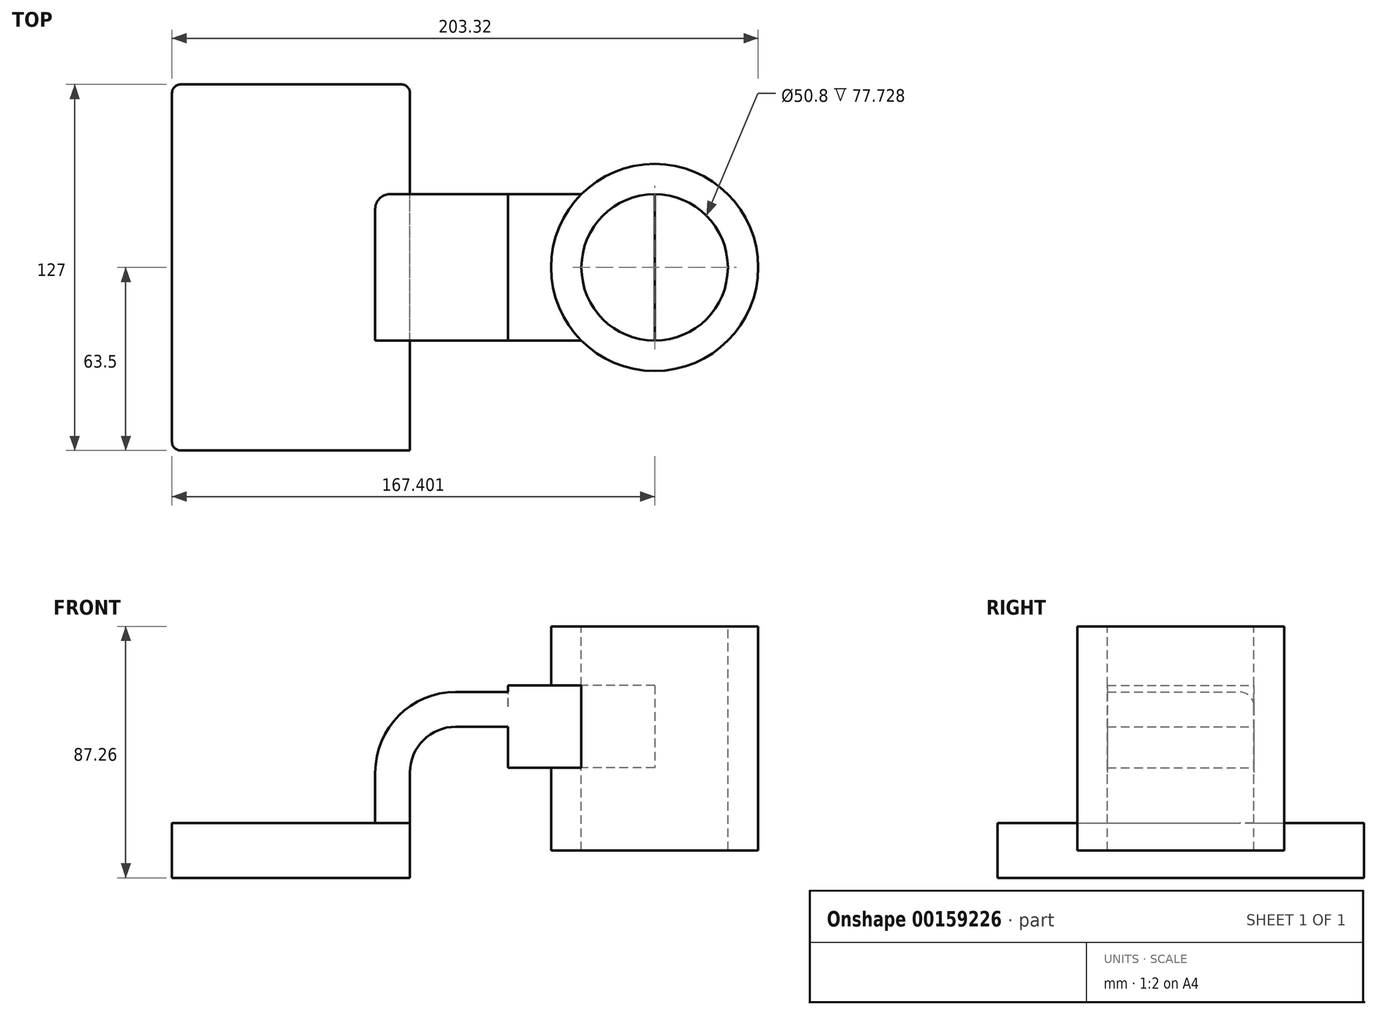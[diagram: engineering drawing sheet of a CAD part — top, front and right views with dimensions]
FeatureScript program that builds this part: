
annotation { "Feature Type Name" : "Feature", "Feature Type Description" : "" }
export const myFeature = defineFeature(function(context is Context, id is Id, definition is map)
    precondition{}
    {
        {
            var Q0;
            Q0=qCreatedBy(makeId("Front.planeOp"),FACE);
            var sketch = newSketch(context, id + "F0", { "sketchPlane" : qUnion([Q0])});
            skLineSegment(sketch, "E0.bottom", {"start": v(-41.28, 9.53) * mm, "end": v(41.28, 9.53) * mm});
            skLineSegment(sketch, "E0.top", {"start": v(-41.28, -9.53) * mm, "end": v(41.28, -9.53) * mm});
            skLineSegment(sketch, "E0.left", {"start": v(-41.28, 9.53) * mm, "end": v(-41.28, -9.53) * mm});
            skLineSegment(sketch, "E0.right", {"start": v(41.28, 9.53) * mm, "end": v(41.28, -9.53) * mm});
            skPoint(sketch, "E0.middle", {"position": v(0, 0) * mm});
            skLineSegment(sketch, "E1.bottom", {"start": v(126.12, 57.16) * mm, "end": v(75.32, 57.16) * mm});
            skLineSegment(sketch, "E1.top", {"start": v(126.12, 28.59) * mm, "end": v(75.32, 28.59) * mm});
            skLineSegment(sketch, "E1.left", {"start": v(126.12, 57.16) * mm, "end": v(126.12, 28.59) * mm});
            skLineSegment(sketch, "E1.right", {"start": v(75.32, 57.16) * mm, "end": v(75.32, 28.59) * mm});
            skPoint(sketch, "E1.middle", {"position": v(100.72, 42.88) * mm});
            skLineSegment(sketch, "E2", {"start": v(41.28, 9.53) * mm, "end": v(41.28, 27) * mm});
            skArc(sketch, "E3", {"start": v(41.28, 27) * mm, "mid": v(45.92, 38.23) * mm, "end": v(57.15, 42.88) * mm});
            skPoint(sketch, "E3.endSnap0", {"position": v(75.32, 42.88) * mm});
            skLineSegment(sketch, "E4", {"start": v(57.15, 42.88) * mm, "end": v(116.67, 42.88) * mm});
            skPoint(sketch, "E4.endSnap0", {"position": v(126.12, 42.88) * mm});
            skLineSegment(sketch, "E5.0", {"start": v(57.15, 54.94) * mm, "end": v(116.67, 54.94) * mm});
            skArc(sketch, "E5.1", {"start": v(29.2, 27) * mm, "mid": v(37.4, 46.76) * mm, "end": v(57.15, 54.94) * mm});
            skLineSegment(sketch, "E5.2", {"start": v(29.2, 9.53) * mm, "end": v(29.2, 27) * mm});
            skFitSpline(sketch, "E6", {"points": [v(-41.28, 9.53) * mm, v(57.15, 54.94) * mm], "startDerivative": vector(0.35, 105.35) * mm, "endDerivative": vector(158.01, -4.18) * mm});
            skSolve(sketch);
        }
        {
            var Q0;
            Q0=makeQuery(id+"F0.imprint","IMPRINT",FACE,{"disambiguationData":[TD([[makeQuery(id+"F0.imprint","IMPRINT",EDGE,{"derivedFrom":sQuery(id+"F0.wireOp",EDGE,"E0.top")}),1.0]])]});
            extrude(context, id + "F1", {"entities" : qUnion([Q0]), "endBound" : BoundingType.SYMMETRIC, "depth" : 127 * mm});
        }
        {
            var Q0;
            {var subQ2=sQuery(id+"F0.wireOp",EDGE,"E2");Q0=makeQuery(id+"F0.imprint","IMPRINT",FACE,{"disambiguationData":[TD([[makeQuery(id+"F0.imprint","IMPRINT",EDGE,{"derivedFrom":subQ2}),1.0]])]});}
            var Q1;
            {var subQ1=sQuery(id+"F0.wireOp",EDGE,"E1.bottom");Q1=makeQuery(id+"F0.imprint","IMPRINT",FACE,{"disambiguationData":[TD([[makeQuery(id+"F0.imprint","IMPRINT",EDGE,{"derivedFrom":subQ1}),1.0]])]});}
            extrude(context, id + "F2", {"entities" : qUnion([Q0, Q1]), "operationType" : NewBodyOperationType.ADD, "endBound" : BoundingType.SYMMETRIC, "depth" : 50.8 * mm});
        }
        {
            var Q0;
            Q0=makeQuery(id+"F0.imprint","IMPRINT",FACE,{"disambiguationData":[TD([[makeQuery(id+"F0.imprint","IMPRINT",EDGE,{"derivedFrom":sQuery(id+"F0.wireOp",EDGE,"E5.1")}),1.0]])]});
            extrude(context, id + "F3", {"entities" : qUnion([Q0]), "operationType" : NewBodyOperationType.ADD, "endBound" : BoundingType.SYMMETRIC, "depth" : 15.88 * mm});
        }
        {
            var Q0;
            Q0=makeQuery(id+"F2.opExtrude","CAP_FACE",FACE,{"disambiguationData":[OSD([sQuery(id+"F0.wireOp",EDGE,"E0.bottom"),sQuery(id+"F0.wireOp",EDGE,"E1.bottom"),sQuery(id+"F0.wireOp",EDGE,"E1.top"),sQuery(id+"F0.wireOp",EDGE,"E1.left"),sQuery(id+"F0.wireOp",EDGE,"E1.right"),sQuery(id+"F0.wireOp",EDGE,"E2"),sQuery(id+"F0.wireOp",EDGE,"E3"),sQuery(id+"F0.wireOp",EDGE,"E4"),sQuery(id+"F0.wireOp",EDGE,"E5.0"),sQuery(id+"F0.wireOp",EDGE,"E5.1"),sQuery(id+"F0.wireOp",EDGE,"E5.2")])],"isStart":false});
            var sketch = newSketch(context, id + "F4", { "sketchPlane" : qUnion([Q0])});
            skPoint(sketch, "E7.oppositeSnap0", {"position": v(100.72, 28.59) * mm});
            skLineSegment(sketch, "E7.bottom", {"start": v(126.12, 77.73) * mm, "end": v(100.72, 77.73) * mm});
            skLineSegment(sketch, "E7.top", {"start": v(126.12, 0) * mm, "end": v(100.72, 0) * mm});
            skLineSegment(sketch, "E7.left", {"start": v(126.12, 77.73) * mm, "end": v(126.12, 0) * mm});
            skLineSegment(sketch, "E7.right", {"start": v(100.72, 77.73) * mm, "end": v(100.72, 0) * mm});
            skSolve(sketch);
        }
        {
            var Q0;
            {var subQ0=sQuery(id+"F4.wireOp",EDGE,"E7.top");Q0=makeQuery(id+"F4.imprint","IMPRINT",FACE,{"disambiguationData":[TD([[makeQuery(id+"F4.imprint","IMPRINT",EDGE,{"derivedFrom":subQ0}),-1.0]])]});}
            var Q1;
            {var subQ0=sQuery(id+"F4.wireOp",EDGE,"E7.left");var subQ1=makeQuery(id+"F2.opExtrude","CAP_EDGE",EDGE,{"disambiguationData":[OSD([sQuery(id+"F0.wireOp",EDGE,"E1.bottom")])],"isStart":false});var subQ2=makeQuery(id+"F4.imprint","INTERSECT",VERTEX,{"derivedFrom":[subQ1,subQ0]});Q1=makeQuery(id+"F4.imprint","IMPRINT",FACE,{"disambiguationData":[TD([[makeQuery(id+"F4.imprint","IMPRINT",EDGE,{"disambiguationData":[TD([[subQ2,-1.0]])],"derivedFrom":subQ0}),-1.0]])]});}
            var Q2;
            {var subQ0=sQuery(id+"F4.wireOp",EDGE,"E7.bottom");Q2=makeQuery(id+"F4.imprint","IMPRINT",FACE,{"disambiguationData":[TD([[makeQuery(id+"F4.imprint","IMPRINT",EDGE,{"derivedFrom":subQ0}),1.0]])]});}
            var Q3;
            Q3=sQuery(id+"F0.wireOp",EDGE,"E1.left");
            revolve(context, id + "F5", {"operationType" : NewBodyOperationType.ADD, "entities" : qUnion([Q0, Q1, Q2]), "axis" : qUnion([Q3]), "revolveType" : RevolveType.FULL});
        }
        {
            var Q0;
            Q0=makeQuery(id+"F1.opExtrude","CAP_EDGE",EDGE,{"disambiguationData":[OSD([sQuery(id+"F0.wireOp",EDGE,"E0.left")])],"isStart":true});
            var Q1;
            Q1=makeQuery(id+"F1.opExtrude","CAP_EDGE",EDGE,{"disambiguationData":[OSD([sQuery(id+"F0.wireOp",EDGE,"E0.right")])],"isStart":true});
            var Q2;
            Q2=makeQuery(id+"F1.opExtrude","CAP_EDGE",EDGE,{"disambiguationData":[OSD([sQuery(id+"F0.wireOp",EDGE,"E0.left")])],"isStart":false});
            fillet(context, id + "F6", {"entities" : qUnion([Q0, Q1, Q2]), "radius" : 3 * mm, "tangentPropagation" : true, "allowEdgeOverflow" : false});
        }
        {
            var Q0;
            Q0=makeQuery(id+"F2.opExtrude","CAP_EDGE",EDGE,{"disambiguationData":[OSD([sQuery(id+"F0.wireOp",EDGE,"E5.1")])],"isStart":true});
            fillet(context, id + "F7", {"entities" : qUnion([Q0]), "radius" : 5.08 * mm, "tangentPropagation" : true, "allowEdgeOverflow" : false});
        }
    });
